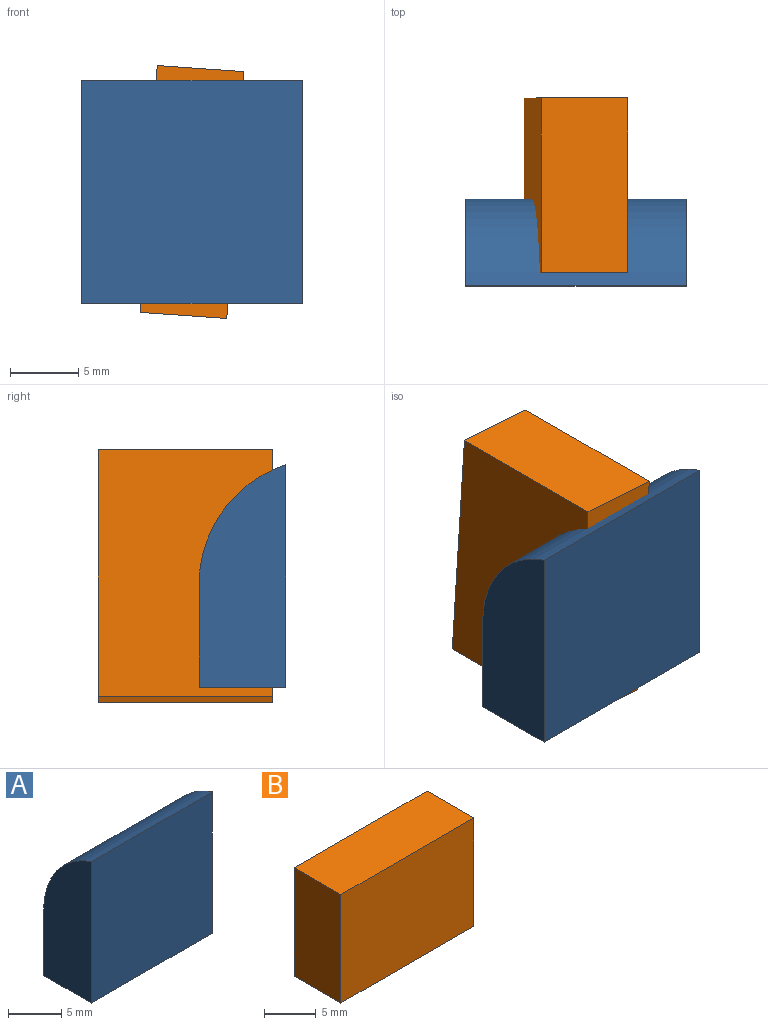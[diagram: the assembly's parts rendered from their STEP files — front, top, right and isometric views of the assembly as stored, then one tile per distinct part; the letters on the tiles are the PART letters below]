
ASSEMBLY  parts=2 mates=1
PART A: 6 faces, bbox 16.1x6.4x16.3 mm
  f0: plane 16.28x6.35mm, normal (1,0,0), area 88.5mm2, adj f2,f3,f4,f5
  f1: plane 16.28x6.35mm, normal (-1,0,0), area 88.5mm2, adj f2,f3,f4,f5
  f2: plane 16.1x6.35mm, normal (0,0,-1), area 102.2mm2, adj f0,f1,f3,f4
  f3: plane 16.28x16.1mm, normal (0,-1,0), area 262mm2, adj f0,f1,f2,f5
  f4: plane 16.1x7.53mm, normal (0,1,0), area 121.2mm2, adj f0,f1,f2,f5
  f5: cylinder r=9.2mm len=16.1mm, axis (-1,0,0), area 186mm2, adj f0,f1,f3,f4
PART B: 6 faces, bbox 18.1x6.4x12.8 mm
  f0: plane 18.09x6.35mm, normal (0,0,-1), area 114.9mm2, adj f1,f3,f4,f5
  f1: plane 12.78x6.35mm, normal (1,0,0), area 81.1mm2, adj f0,f2,f4,f5
  f2: plane 18.09x6.35mm, normal (0,0,1), area 114.9mm2, adj f1,f3,f4,f5
  f3: plane 12.78x6.35mm, normal (-1,0,0), area 81.1mm2, adj f0,f2,f4,f5
  f4: plane 18.09x12.78mm, normal (0,-1,0), area 231.2mm2, adj f0,f1,f2,f3
  f5: plane 18.09x12.78mm, normal (0,1,0), area 231.2mm2, adj f0,f1,f2,f3
PLACE A t=(-5.95,-1.25,1.31)mm fixed
PLACE B rot(axis=(-0.6,-0.56,-0.56),117.7deg) t=(-1.7,24.44,0.64)mm
MATE cylindrical B.f2 <-> A.f3  axis (0,1,0) through (2.1,12.49,9.45)mm
